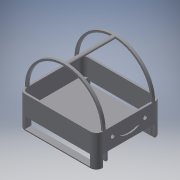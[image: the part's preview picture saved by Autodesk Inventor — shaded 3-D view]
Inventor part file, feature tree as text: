
AUTODESK INVENTOR PART (.ipt)
format: ipt  version: 2019 (Build 230136000, 136)  size: 337,920 bytes
history: native  units: in
note: dims shown in document units (in); Inventor stores cm internally (conversion verified against a paired STEP export)
features: sketch x12, extrude x9, plane x3, sweep x2, fillet x2, shell x1, revolve x1
ambient origin geometry x8: Origin, YZ Plane, XZ Plane, XY Plane, X Axis, Y Axis, Z Axis, Center Point
bodies: Solid1 (feature_tree)
feature tree (30):
  extrude  "Extrusion1"  Depth=6.0in
  shell  "Shell1"  Thickness=0.5in
  plane  "Work Plane1"
  sweep  "Sweep1"
  plane  "Work Plane2"
  sketch  "Sketch7"  dims[d11=90.0deg d12=0.35in d13=0.15in]
  revolve  "Revolution1"  [1 undecoded]
  plane  "Work Plane3"
  sweep  "Sweep2"
  fillet  "Fillet1"  Radius=0.15in
  extrude  "Extrusion2"  TaperAngle=0.0deg  [1 undecoded]
  sketch  "Sketch13"  dims[d22=0.75in d23=0.25in d24=0.0in]
  extrude  "Extrusion3"  Depth=0.125in TaperAngle=0.0deg
  extrude  "Extrusion4"  Depth=0.75in
  extrude  "Extrusion5"  Depth=0.25in TaperAngle=0.0deg
  extrude  "Extrusion6"  Depth=0.1in TaperAngle=0.0deg
  extrude  "Extrusion7"  Depth=0.15in TaperAngle=0.0deg
  fillet  "Fillet2"  Radius=0.125in
  extrude  "Extrusion8"  Depth=0.15in
  extrude  "Extrusion9"  Depth=4.75in
  sketch  "Sketch1"  dims[d0=6.0in d1=5.0in d2=0.5in]
  sketch  "Sketch2"  dims[d3=1.5in d4=0.0in d5=0.15in]
  sketch  "Sketch4"  dims[d6=0.2in d7=0.0in d8=0.0in]
  sketch  "Sketch10"  dims[d14=0.175in d15=0.0in d16=0.0in]
  sketch  "Sketch11"  dims[d17=0.125in d18=0.4in d19=0.0in]
  sketch  "Sketch12"  dims[d20=0.3in d21=0.75in]
  sketch  "Sketch14"  dims[d25=0.05in d26=0.0in d27=0.1in d28=0.0in]
  sketch  "Sketch15"  dims[d29=1.0in d30=0.0in d31=0.15in d32=0.0in d33=0.125in]
  sketch  "Sketch16"  dims[d36=6.0in d37=0.15in]
  sketch  "Sketch17"  dims[d38=0.15in d39=0.2in d40=0.2in d41=0.6in d42=0.0in d43=0.15in d44=1.25in d45=4.75in d46=0.0in d47=0.0in]
note: 2 required parameter values undecoded (feature->parameter linkage not recoverable at this tier; creation-order binding heuristic only, values carry confidence <= 0.55)